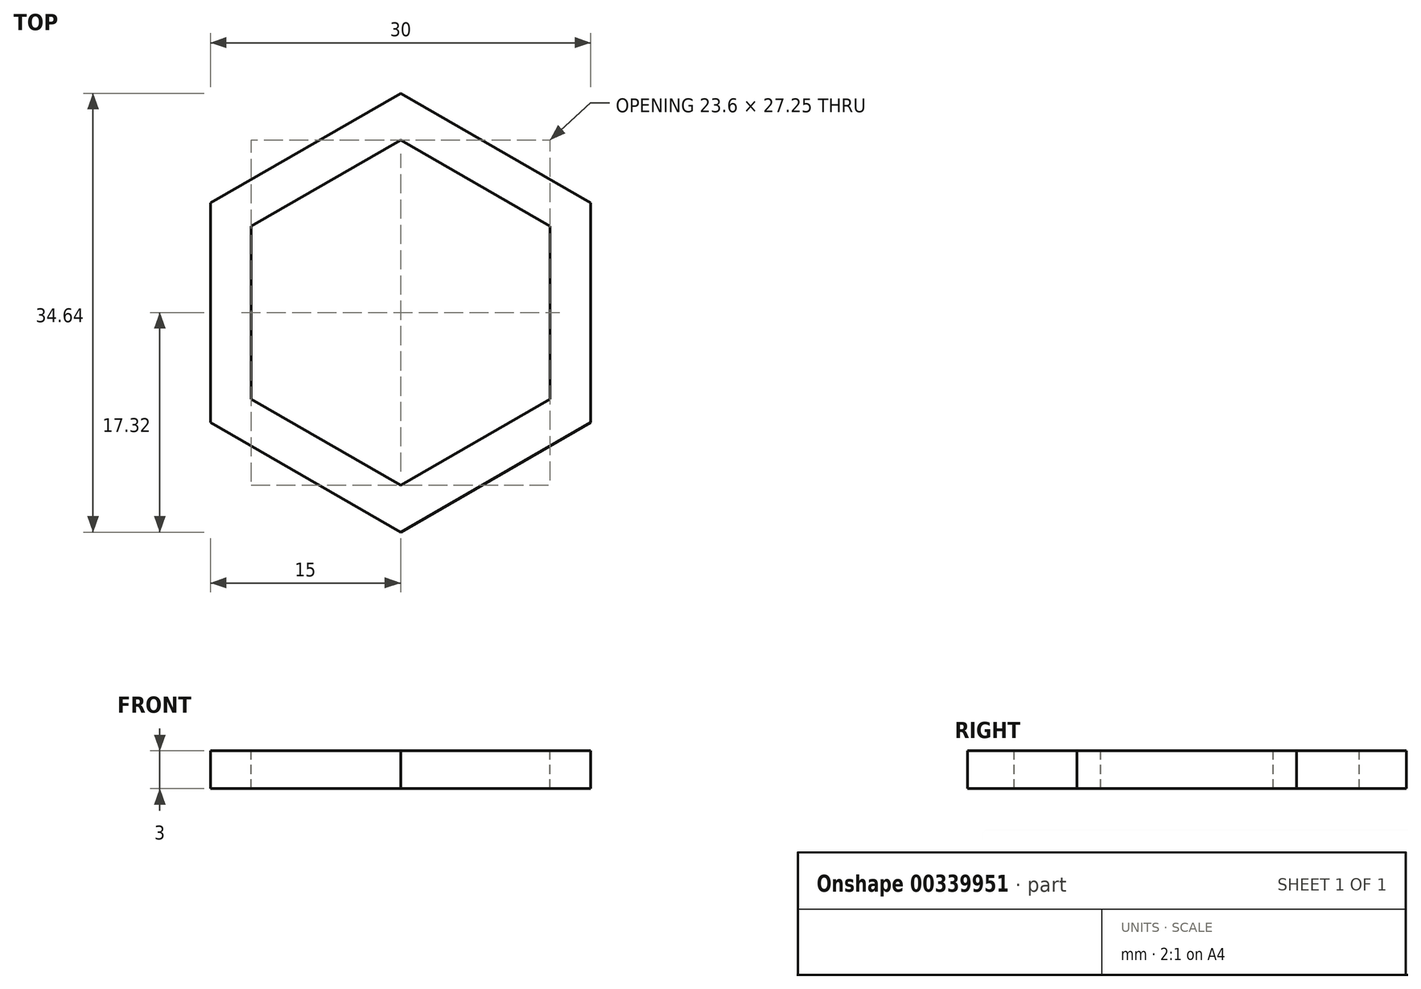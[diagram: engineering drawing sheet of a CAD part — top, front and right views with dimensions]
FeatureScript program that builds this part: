
annotation { "Feature Type Name" : "Feature", "Feature Type Description" : "" }
export const myFeature = defineFeature(function(context is Context, id is Id, definition is map)
    precondition{}
    {
        {
            var Q0;
            Q0=qCreatedBy(makeId("Top.planeOp"),FACE);
            var sketch = newSketch(context, id + "F0", { "sketchPlane" : qUnion([Q0])});
            skCircle(sketch, "E0.cCircle", {"center": v(0, 0) * mm, "radius": 15 * mm, "construction": true});
            skLineSegment(sketch, "E0.0", {"start": v(15, 8.66) * mm, "end": v(15, -8.66) * mm});
            skLineSegment(sketch, "E0.1", {"start": v(15, -8.66) * mm, "end": v(0, -17.32) * mm});
            skLineSegment(sketch, "E0.2", {"start": v(0, -17.32) * mm, "end": v(-15, -8.66) * mm});
            skLineSegment(sketch, "E0.3", {"start": v(-15, -8.66) * mm, "end": v(-15, 8.66) * mm});
            skLineSegment(sketch, "E0.4", {"start": v(-15, 8.66) * mm, "end": v(0, 17.32) * mm});
            skLineSegment(sketch, "E0.5", {"start": v(0, 17.32) * mm, "end": v(15, 8.66) * mm});
            skPoint(sketch, "E0.0.midPoint", {"position": v(15, 0) * mm});
            skSolve(sketch);
        }
        {
            var Q0;
            Q0 = qSketchRegion(id + "F0", true);
            extrude(context, id + "F1", {"entities" : qUnion([Q0]), "depth" : 3 * mm, "offsetDistance" : 25 * mm});
        }
        {
            var Q0;
            Q0=makeQuery(id+"F1.opExtrude","CAP_FACE",FACE,{"disambiguationData":[OSD([sQuery(id+"F0.wireOp",EDGE,"E0.0"),sQuery(id+"F0.wireOp",EDGE,"E0.1"),sQuery(id+"F0.wireOp",EDGE,"E0.2"),sQuery(id+"F0.wireOp",EDGE,"E0.3"),sQuery(id+"F0.wireOp",EDGE,"E0.4"),sQuery(id+"F0.wireOp",EDGE,"E0.5")])],"isStart":false});
            var sketch = newSketch(context, id + "F2", { "sketchPlane" : qUnion([Q0])});
            skLineSegment(sketch, "E1.0", {"start": v(11.8, -6.81) * mm, "end": v(11.8, 6.81) * mm});
            skLineSegment(sketch, "E1.1", {"start": v(0, 13.63) * mm, "end": v(-11.8, 6.81) * mm});
            skLineSegment(sketch, "E1.2", {"start": v(-11.8, 6.81) * mm, "end": v(-11.8, -6.81) * mm});
            skLineSegment(sketch, "E1.3", {"start": v(11.8, 6.81) * mm, "end": v(0, 13.63) * mm});
            skLineSegment(sketch, "E1.4", {"start": v(-11.8, -6.81) * mm, "end": v(0, -13.63) * mm});
            skLineSegment(sketch, "E1.5", {"start": v(0, -13.63) * mm, "end": v(11.8, -6.81) * mm});
            skSolve(sketch);
        }
        {
            var Q0;
            Q0 = qSketchRegion(id + "F2", true);
            extrude(context, id + "F3", {"entities" : qUnion([Q0]), "operationType" : NewBodyOperationType.REMOVE, "oppositeDirection" : true, "depth" : 25 * mm, "offsetDistance" : 25 * mm});
        }
    });
